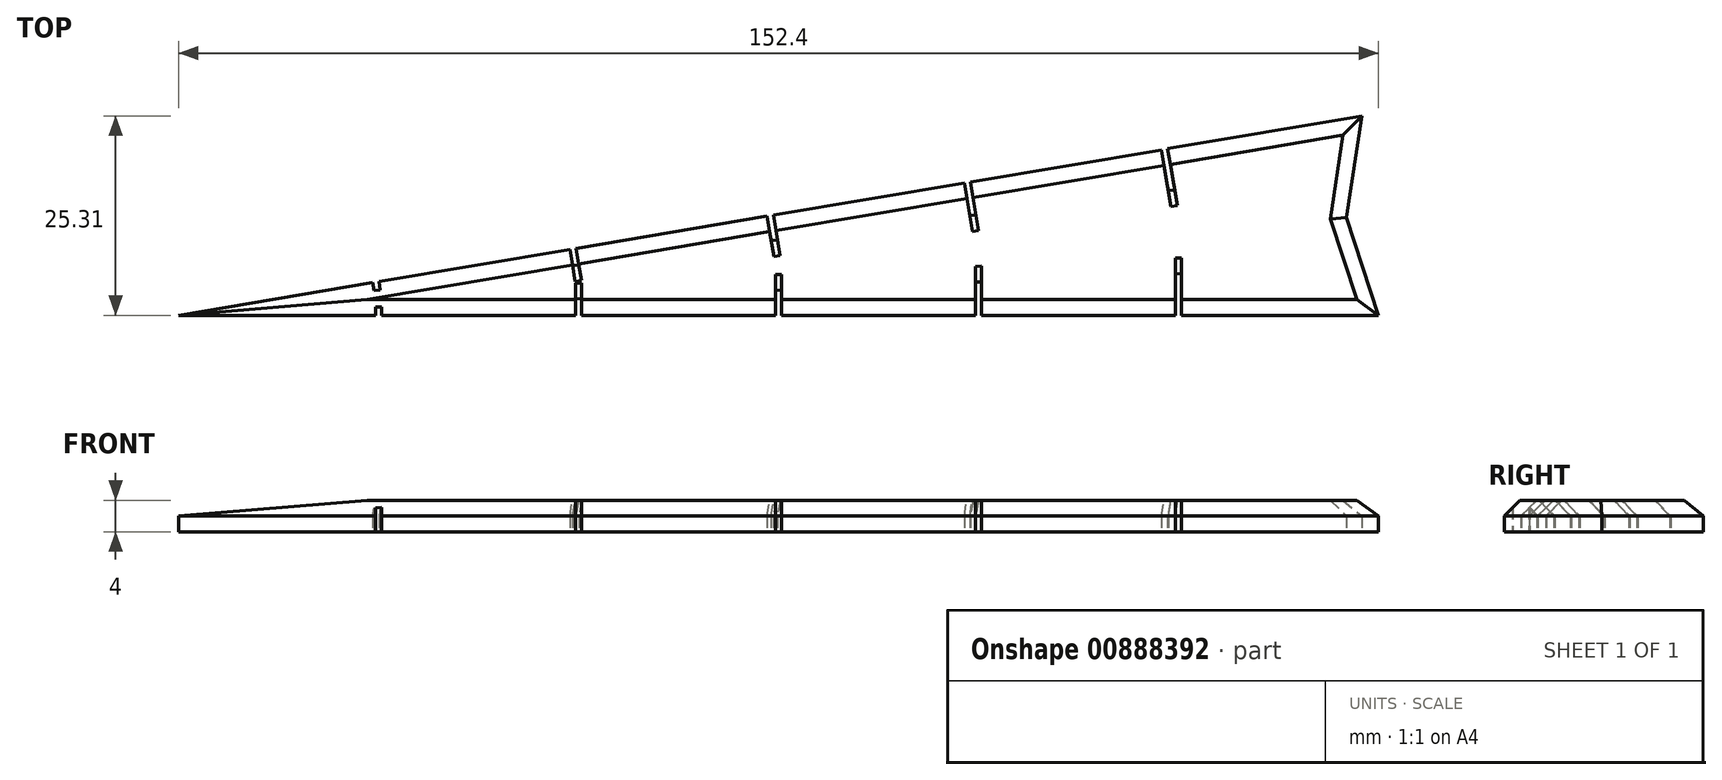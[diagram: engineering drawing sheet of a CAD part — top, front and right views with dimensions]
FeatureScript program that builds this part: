
annotation { "Feature Type Name" : "Feature", "Feature Type Description" : "" }
export const myFeature = defineFeature(function(context is Context, id is Id, definition is map)
    precondition{}
    {
        {
            var Q0;
            Q0=qCreatedBy(makeId("Top.planeOp"),FACE);
            var sketch = newSketch(context, id + "F0", { "sketchPlane" : qUnion([Q0])});
            skCircle(sketch, "E0", {"center": v(0, 0) * mm, "radius": 76.5 * mm, "construction": true});
            skLineSegment(sketch, "E1", {"start": v(-12.7, -75.44) * mm, "end": v(-1, 76.5) * mm});
            skPoint(sketch, "E2", {"position": v(0, 76.5) * mm});
            skLineSegment(sketch, "E3", {"start": v(0, -72.44) * mm, "end": v(-12.7, -75.44) * mm});
            skLineSegment(sketch, "E4", {"start": v(-10.78, -50.52) * mm, "end": v(-5.38, -50.93) * mm});
            skLineSegment(sketch, "E5", {"start": v(-5.35, -50.13) * mm, "end": v(-10.72, -49.72) * mm});
            skLineSegment(sketch, "E6", {"start": v(-6.1, -67.89) * mm, "end": v(0, -66.44) * mm, "construction": true});
            skLineSegment(sketch, "E7", {"start": v(-6.1, -67.89) * mm, "end": v(0, 76.5) * mm, "construction": true});
            skLineSegment(sketch, "E8", {"start": v(-5.35, -50.13) * mm, "end": v(-5.38, -50.93) * mm});
            skLineSegment(sketch, "E9", {"start": v(-10.78, -50.52) * mm, "end": v(-10.72, -49.72) * mm});
            skPoint(sketch, "E10", {"position": v(-10.75, -50.12) * mm});
            skLineSegment(sketch, "E11", {"start": v(-1, 76.5) * mm, "end": v(0, 76.5) * mm});
            skLineSegment(sketch, "E12", {"start": v(0, 76.5) * mm, "end": v(0, -72.44) * mm, "construction": true});
            skLineSegment(sketch, "E13.MirrorCS", {"start": v(1, 76.5) * mm, "end": v(0, 76.5) * mm});
            skLineSegment(sketch, "E14.MirrorCS", {"start": v(12.7, -75.44) * mm, "end": v(1, 76.5) * mm});
            skLineSegment(sketch, "E15.MirrorCS", {"start": v(0, -72.44) * mm, "end": v(12.7, -75.44) * mm});
            skSolve(sketch);
        }
        {
            var Q0;
            Q0=qCreatedBy(makeId("Top.planeOp"),FACE);
            var sketch = newSketch(context, id + "F1", { "sketchPlane" : qUnion([Q0])});
            skLineSegment(sketch, "E16", {"start": v(0, 0) * mm, "end": v(-152.4, 0) * mm});
            skLineSegment(sketch, "E17", {"start": v(-152.4, 0) * mm, "end": v(-1.06, 12.66) * mm});
            skLineSegment(sketch, "E18", {"start": v(-1.06, 12.66) * mm, "end": v(0, 0) * mm});
            skLineSegment(sketch, "E19", {"start": v(0, 0) * mm, "end": v(-4.05, 12.4) * mm});
            skLineSegment(sketch, "E20", {"start": v(-152.4, 0) * mm, "end": v(-0.53, 6.33) * mm});
            skPoint(sketch, "E20.endSnap0", {"position": v(-0.53, 6.33) * mm});
            skLineSegment(sketch, "E21.bottom", {"start": v(-25.8, 7.7) * mm, "end": v(-25, 7.7) * mm});
            skLineSegment(sketch, "E21.top", {"start": v(-25.8, 0) * mm, "end": v(-25, 0) * mm});
            skLineSegment(sketch, "E21.left", {"start": v(-25.8, 7.7) * mm, "end": v(-25.8, 0) * mm});
            skLineSegment(sketch, "E21.right", {"start": v(-25, 7.7) * mm, "end": v(-25, 0) * mm});
            skPoint(sketch, "E21.middle", {"position": v(-25.4, 3.85) * mm});
            skPoint(sketch, "E22.1.0.0", {"position": v(-50.8, 3.85) * mm});
            skLineSegment(sketch, "E22.1.0.1", {"start": v(-51.2, 7.7) * mm, "end": v(-51.2, 0) * mm});
            skLineSegment(sketch, "E22.1.0.2", {"start": v(-50.4, 7.7) * mm, "end": v(-50.4, 0) * mm});
            skLineSegment(sketch, "E22.1.0.3", {"start": v(-51.2, 0) * mm, "end": v(-50.4, 0) * mm});
            skLineSegment(sketch, "E22.1.0.4", {"start": v(-51.2, 7.7) * mm, "end": v(-50.4, 7.7) * mm});
            skPoint(sketch, "E22.2.0.0", {"position": v(-76.2, 3.85) * mm});
            skLineSegment(sketch, "E22.2.0.1", {"start": v(-76.6, 7.7) * mm, "end": v(-76.6, 0) * mm});
            skLineSegment(sketch, "E22.2.0.2", {"start": v(-75.8, 7.7) * mm, "end": v(-75.8, 0) * mm});
            skLineSegment(sketch, "E22.2.0.3", {"start": v(-76.6, 0) * mm, "end": v(-75.8, 0) * mm});
            skLineSegment(sketch, "E22.2.0.4", {"start": v(-76.6, 7.7) * mm, "end": v(-75.8, 7.7) * mm});
            skPoint(sketch, "E22.3.0.0", {"position": v(-101.6, 3.85) * mm});
            skLineSegment(sketch, "E22.3.0.1", {"start": v(-102, 7.7) * mm, "end": v(-102, 0) * mm});
            skLineSegment(sketch, "E22.3.0.2", {"start": v(-101.2, 7.7) * mm, "end": v(-101.2, 0) * mm});
            skLineSegment(sketch, "E22.3.0.3", {"start": v(-102, 0) * mm, "end": v(-101.2, 0) * mm});
            skLineSegment(sketch, "E22.3.0.4", {"start": v(-102, 7.7) * mm, "end": v(-101.2, 7.7) * mm});
            skPoint(sketch, "E22.4.0.0", {"position": v(-127, 3.85) * mm});
            skLineSegment(sketch, "E22.4.0.1", {"start": v(-127.4, 7.7) * mm, "end": v(-127.4, 0) * mm});
            skLineSegment(sketch, "E22.4.0.2", {"start": v(-126.6, 7.7) * mm, "end": v(-126.6, 0) * mm});
            skLineSegment(sketch, "E22.4.0.3", {"start": v(-127.4, 0) * mm, "end": v(-126.6, 0) * mm});
            skLineSegment(sketch, "E22.4.0.4", {"start": v(-127.4, 7.7) * mm, "end": v(-126.6, 7.7) * mm});
            skLineSegment(sketch, "E22.direction1", {"start": v(-25.8, 0) * mm, "end": v(-51.2, 0) * mm, "construction": true});
            skSolve(sketch);
        }
        {
            var Q0;
            {var subQ0=sQuery(id+"F1.wireOp",EDGE,"E19");var subQ5=sQuery(id+"F1.wireOp",EDGE,"E20");var subQ7=makeQuery(id+"F1.imprint","INTERSECT",VERTEX,{"derivedFrom":[subQ0,subQ5]});Q0=makeQuery(id+"F1.imprint","IMPRINT",FACE,{"disambiguationData":[TD([[makeQuery(id+"F1.imprint","IMPRINT",EDGE,{"disambiguationData":[TD([[subQ7,1.0]])],"derivedFrom":subQ5}),-1.0]])]});}
            var Q1;
            {var subQ7=sQuery(id+"F1.wireOp",EDGE,"E21.bottom");Q1=makeQuery(id+"F1.imprint","IMPRINT",FACE,{"disambiguationData":[TD([[makeQuery(id+"F1.imprint","IMPRINT",EDGE,{"derivedFrom":subQ7}),1.0]])]});}
            var Q2;
            {var subQ3=sQuery(id+"F1.wireOp",EDGE,"E22.1.0.2");var subQ5=sQuery(id+"F1.wireOp",EDGE,"E20");var subQ6=makeQuery(id+"F1.imprint","INTERSECT",VERTEX,{"derivedFrom":[subQ5,subQ3]});Q2=makeQuery(id+"F1.imprint","IMPRINT",FACE,{"disambiguationData":[TD([[makeQuery(id+"F1.imprint","IMPRINT",EDGE,{"disambiguationData":[TD([[subQ6,-1.0]])],"derivedFrom":subQ5}),-1.0]])]});}
            var Q3;
            {var subQ3=sQuery(id+"F1.wireOp",EDGE,"E22.2.0.2");var subQ5=sQuery(id+"F1.wireOp",EDGE,"E20");var subQ7=makeQuery(id+"F1.imprint","INTERSECT",VERTEX,{"derivedFrom":[subQ5,subQ3]});Q3=makeQuery(id+"F1.imprint","IMPRINT",FACE,{"disambiguationData":[TD([[makeQuery(id+"F1.imprint","IMPRINT",EDGE,{"disambiguationData":[TD([[subQ7,-1.0]])],"derivedFrom":subQ5}),-1.0]])]});}
            var Q4;
            {var subQ5=sQuery(id+"F1.wireOp",EDGE,"E22.1.0.4");Q4=makeQuery(id+"F1.imprint","IMPRINT",FACE,{"disambiguationData":[TD([[makeQuery(id+"F1.imprint","IMPRINT",EDGE,{"derivedFrom":subQ5}),-1.0]])]});}
            var Q5;
            {var subQ5=sQuery(id+"F1.wireOp",EDGE,"E21.bottom");Q5=makeQuery(id+"F1.imprint","IMPRINT",FACE,{"disambiguationData":[TD([[makeQuery(id+"F1.imprint","IMPRINT",EDGE,{"derivedFrom":subQ5}),-1.0]])]});}
            var Q6;
            {var subQ0=sQuery(id+"F1.wireOp",EDGE,"E22.3.0.2");var subQ1=sQuery(id+"F1.wireOp",EDGE,"E17");var subQ2=makeQuery(id+"F1.imprint","INTERSECT",VERTEX,{"derivedFrom":[subQ1,subQ0]});Q6=makeQuery(id+"F1.imprint","IMPRINT",FACE,{"disambiguationData":[TD([[makeQuery(id+"F1.imprint","IMPRINT",EDGE,{"disambiguationData":[TD([[subQ2,-1.0]])],"derivedFrom":subQ1}),-1.0]])]});}
            var Q7;
            {var subQ0=sQuery(id+"F1.wireOp",EDGE,"E22.2.0.1");var subQ1=sQuery(id+"F1.wireOp",EDGE,"E17");var subQ2=makeQuery(id+"F1.imprint","INTERSECT",VERTEX,{"derivedFrom":[subQ1,subQ0]});Q7=makeQuery(id+"F1.imprint","IMPRINT",FACE,{"disambiguationData":[TD([[makeQuery(id+"F1.imprint","IMPRINT",EDGE,{"disambiguationData":[TD([[subQ2,-1.0]])],"derivedFrom":subQ1}),-1.0]])]});}
            var Q8;
            {var subQ3=sQuery(id+"F1.wireOp",EDGE,"E22.3.0.2");var subQ5=sQuery(id+"F1.wireOp",EDGE,"E20");var subQ6=makeQuery(id+"F1.imprint","INTERSECT",VERTEX,{"derivedFrom":[subQ5,subQ3]});Q8=makeQuery(id+"F1.imprint","IMPRINT",FACE,{"disambiguationData":[TD([[makeQuery(id+"F1.imprint","IMPRINT",EDGE,{"disambiguationData":[TD([[subQ6,-1.0]])],"derivedFrom":subQ5}),-1.0]])]});}
            var Q9;
            {var subQ0=sQuery(id+"F1.wireOp",EDGE,"E22.3.0.1");var subQ1=sQuery(id+"F1.wireOp",EDGE,"E17");var subQ2=makeQuery(id+"F1.imprint","INTERSECT",VERTEX,{"derivedFrom":[subQ1,subQ0]});Q9=makeQuery(id+"F1.imprint","IMPRINT",FACE,{"disambiguationData":[TD([[makeQuery(id+"F1.imprint","IMPRINT",EDGE,{"disambiguationData":[TD([[subQ2,-1.0]])],"derivedFrom":subQ1}),-1.0]])]});}
            var Q10;
            {var subQ3=sQuery(id+"F1.wireOp",EDGE,"E22.4.0.2");var subQ5=sQuery(id+"F1.wireOp",EDGE,"E20");var subQ6=makeQuery(id+"F1.imprint","INTERSECT",VERTEX,{"derivedFrom":[subQ5,subQ3]});Q10=makeQuery(id+"F1.imprint","IMPRINT",FACE,{"disambiguationData":[TD([[makeQuery(id+"F1.imprint","IMPRINT",EDGE,{"disambiguationData":[TD([[subQ6,-1.0]])],"derivedFrom":subQ5}),-1.0]])]});}
            var Q11;
            {var subQ0=sQuery(id+"F1.wireOp",EDGE,"E22.4.0.2");var subQ1=sQuery(id+"F1.wireOp",EDGE,"E17");var subQ2=makeQuery(id+"F1.imprint","INTERSECT",VERTEX,{"derivedFrom":[subQ1,subQ0]});Q11=makeQuery(id+"F1.imprint","IMPRINT",FACE,{"disambiguationData":[TD([[makeQuery(id+"F1.imprint","IMPRINT",EDGE,{"disambiguationData":[TD([[subQ2,-1.0]])],"derivedFrom":subQ1}),-1.0]])]});}
            var Q12;
            {var subQ0=sQuery(id+"F1.wireOp",EDGE,"E22.4.0.1");var subQ1=sQuery(id+"F1.wireOp",EDGE,"E17");var subQ2=makeQuery(id+"F1.imprint","INTERSECT",VERTEX,{"derivedFrom":[subQ1,subQ0]});Q12=makeQuery(id+"F1.imprint","IMPRINT",FACE,{"disambiguationData":[TD([[makeQuery(id+"F1.imprint","IMPRINT",EDGE,{"disambiguationData":[TD([[subQ2,-1.0]])],"derivedFrom":subQ1}),-1.0]])]});}
            var Q13;
            {var subQ1=sQuery(id+"F1.wireOp",EDGE,"E17");var subQ3=sQuery(id+"F1.wireOp",EDGE,"E22.4.0.1");var subQ4=makeQuery(id+"F1.imprint","INTERSECT",VERTEX,{"derivedFrom":[subQ1,subQ3]});Q13=makeQuery(id+"F1.imprint","IMPRINT",FACE,{"disambiguationData":[TD([[makeQuery(id+"F1.imprint","IMPRINT",EDGE,{"disambiguationData":[TD([[subQ4,-1.0]])],"derivedFrom":subQ3}),-1.0]])]});}
            var Q14;
            {var subQ0=sQuery(id+"F1.wireOp",EDGE,"E20");var subQ3=sQuery(id+"F1.wireOp",EDGE,"E22.4.0.1");var subQ5=makeQuery(id+"F1.imprint","INTERSECT",VERTEX,{"derivedFrom":[subQ0,subQ3]});Q14=makeQuery(id+"F1.imprint","IMPRINT",FACE,{"disambiguationData":[TD([[makeQuery(id+"F1.imprint","IMPRINT",EDGE,{"disambiguationData":[TD([[subQ5,1.0]])],"derivedFrom":subQ0}),-1.0]])]});}
            extrude(context, id + "F2", {"entities" : qUnion([Q0, Q1, Q2, Q3, Q4, Q5, Q6, Q7, Q8, Q9, Q10, Q11, Q12, Q13, Q14]), "depth" : 4 * mm, "offsetDistance" : 25 * mm});
        }
        {
            var Q0;
            {var subQ0=sQuery(id+"F1.wireOp",EDGE,"E16");Q0=makeQuery(id+"F2.opExtrude","CAP_EDGE",EDGE,{"disambiguationData":[OSD([subQ0]),TDD([makeQuery(id+"F1.imprint","IMPRINT",EDGE,{"disambiguationData":[TD([[makeQuery(id+"F1.imprint","INTERSECT",VERTEX,{"derivedFrom":[subQ0,sQuery(id+"F1.wireOp",EDGE,"E17"),sQuery(id+"F1.wireOp",EDGE,"E20")]}),1.0]])],"derivedFrom":subQ0})])],"isStart":false});}
            var Q1;
            {var subQ0=sQuery(id+"F1.wireOp",EDGE,"E16");Q1=makeQuery(id+"F2.opExtrude","CAP_EDGE",EDGE,{"disambiguationData":[OSD([subQ0]),TDD([makeQuery(id+"F1.imprint","IMPRINT",EDGE,{"disambiguationData":[TD([[makeQuery(id+"F1.imprint","INTERSECT",VERTEX,{"derivedFrom":[subQ0,sQuery(id+"F1.wireOp",EDGE,"E22.2.0.1"),sQuery(id+"F1.wireOp",EDGE,"E22.2.0.3")]}),-1.0]])],"derivedFrom":subQ0})])],"isStart":false});}
            var Q2;
            {var subQ0=sQuery(id+"F1.wireOp",EDGE,"E16");Q2=makeQuery(id+"F2.opExtrude","CAP_EDGE",EDGE,{"disambiguationData":[OSD([subQ0]),TDD([makeQuery(id+"F1.imprint","IMPRINT",EDGE,{"disambiguationData":[TD([[makeQuery(id+"F1.imprint","INTERSECT",VERTEX,{"derivedFrom":[subQ0,sQuery(id+"F1.wireOp",EDGE,"E22.1.0.1"),sQuery(id+"F1.wireOp",EDGE,"E22.1.0.3")]}),-1.0]])],"derivedFrom":subQ0})])],"isStart":false});}
            var Q3;
            {var subQ0=sQuery(id+"F1.wireOp",EDGE,"E16");Q3=makeQuery(id+"F2.opExtrude","CAP_EDGE",EDGE,{"disambiguationData":[OSD([subQ0]),TDD([makeQuery(id+"F1.imprint","IMPRINT",EDGE,{"disambiguationData":[TD([[makeQuery(id+"F1.imprint","INTERSECT",VERTEX,{"derivedFrom":[subQ0,sQuery(id+"F1.wireOp",EDGE,"E21.top"),sQuery(id+"F1.wireOp",EDGE,"E21.left")]}),-1.0]])],"derivedFrom":subQ0})])],"isStart":false});}
            var Q4;
            {var subQ0=sQuery(id+"F1.wireOp",EDGE,"E16");Q4=makeQuery(id+"F2.opExtrude","CAP_EDGE",EDGE,{"disambiguationData":[OSD([subQ0]),TDD([makeQuery(id+"F1.imprint","IMPRINT",EDGE,{"disambiguationData":[TD([[makeQuery(id+"F1.imprint","INTERSECT",VERTEX,{"derivedFrom":[subQ0,sQuery(id+"F1.wireOp",EDGE,"E18"),sQuery(id+"F1.wireOp",EDGE,"E19")]}),-1.0]])],"derivedFrom":subQ0})])],"isStart":false});}
            var Q5;
            {var subQ0=sQuery(id+"F1.wireOp",EDGE,"E20");Q5=makeQuery(id+"F2.opExtrude","CAP_EDGE",EDGE,{"disambiguationData":[OSD([subQ0]),TDD([makeQuery(id+"F1.imprint","IMPRINT",EDGE,{"disambiguationData":[TD([[makeQuery(id+"F1.imprint","INTERSECT",VERTEX,{"derivedFrom":[subQ0,sQuery(id+"F1.wireOp",EDGE,"E22.3.0.1")]}),-1.0]])],"derivedFrom":subQ0})])],"isStart":false});}
            var Q6;
            {var subQ0=sQuery(id+"F1.wireOp",EDGE,"E20");Q6=makeQuery(id+"F2.opExtrude","CAP_EDGE",EDGE,{"disambiguationData":[OSD([subQ0]),TDD([makeQuery(id+"F1.imprint","IMPRINT",EDGE,{"disambiguationData":[TD([[makeQuery(id+"F1.imprint","INTERSECT",VERTEX,{"derivedFrom":[subQ0,sQuery(id+"F1.wireOp",EDGE,"E22.2.0.1")]}),-1.0]])],"derivedFrom":subQ0})])],"isStart":false});}
            var Q7;
            {var subQ0=sQuery(id+"F1.wireOp",EDGE,"E20");Q7=makeQuery(id+"F2.opExtrude","CAP_EDGE",EDGE,{"disambiguationData":[OSD([subQ0]),TDD([makeQuery(id+"F1.imprint","IMPRINT",EDGE,{"disambiguationData":[TD([[makeQuery(id+"F1.imprint","INTERSECT",VERTEX,{"derivedFrom":[subQ0,sQuery(id+"F1.wireOp",EDGE,"E22.1.0.1")]}),-1.0]])],"derivedFrom":subQ0})])],"isStart":false});}
            var Q8;
            {var subQ0=sQuery(id+"F1.wireOp",EDGE,"E20");Q8=makeQuery(id+"F2.opExtrude","CAP_EDGE",EDGE,{"disambiguationData":[OSD([subQ0]),TDD([makeQuery(id+"F1.imprint","IMPRINT",EDGE,{"disambiguationData":[TD([[makeQuery(id+"F1.imprint","INTERSECT",VERTEX,{"derivedFrom":[subQ0,sQuery(id+"F1.wireOp",EDGE,"E21.left")]}),-1.0]])],"derivedFrom":subQ0})])],"isStart":false});}
            var Q9;
            Q9=makeQuery(id+"F2.opExtrude","CAP_EDGE",EDGE,{"disambiguationData":[OSD([sQuery(id+"F1.wireOp",EDGE,"E19")])],"isStart":false});
            chamfer(context, id + "F3", {"entities" : qUnion([Q0, Q1, Q2, Q3, Q4, Q5, Q6, Q7, Q8, Q9]), "width" : 2 * mm, "tangentPropagation" : true});
        }
        {
            var Q0;
            Q0=makeQuery(id+"F2.opExtrude","SWEPT_BODY",BODY,{"disambiguationData":[OSD([sQuery(id+"F1.wireOp",EDGE,"E16"),sQuery(id+"F1.wireOp",EDGE,"E17"),sQuery(id+"F1.wireOp",EDGE,"E19"),sQuery(id+"F1.wireOp",EDGE,"E20"),sQuery(id+"F1.wireOp",EDGE,"E21.left"),sQuery(id+"F1.wireOp",EDGE,"E21.right"),sQuery(id+"F1.wireOp",EDGE,"E22.1.0.1"),sQuery(id+"F1.wireOp",EDGE,"E22.1.0.2"),sQuery(id+"F1.wireOp",EDGE,"E22.2.0.1"),sQuery(id+"F1.wireOp",EDGE,"E22.2.0.2"),sQuery(id+"F1.wireOp",EDGE,"E22.3.0.1"),sQuery(id+"F1.wireOp",EDGE,"E22.3.0.2"),sQuery(id+"F1.wireOp",EDGE,"E22.4.0.1"),sQuery(id+"F1.wireOp",EDGE,"E22.4.0.2")])]});
            var Q1;
            Q1=makeQuery(id+"F2.opExtrude","SWEPT_FACE",FACE,{"disambiguationData":[OSD([sQuery(id+"F1.wireOp",EDGE,"E17")])]});
            mirror(context, id + "F4", {"operationType" : NewBodyOperationType.ADD, "entities" : qUnion([Q0]), "mirrorPlane" : qUnion([Q1])});
        }
    });
